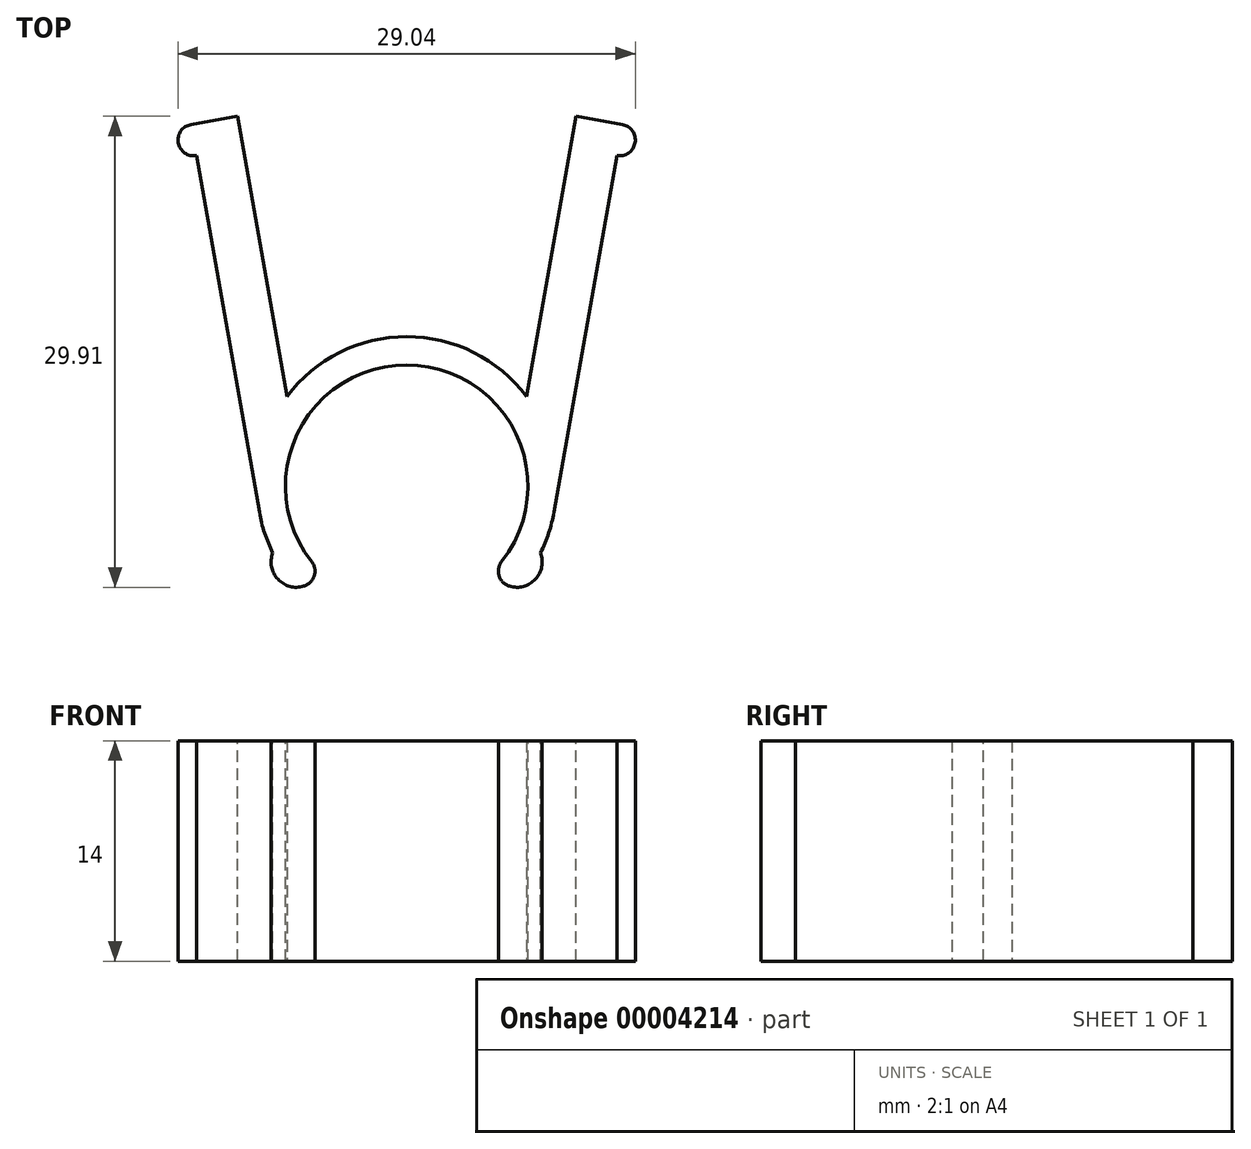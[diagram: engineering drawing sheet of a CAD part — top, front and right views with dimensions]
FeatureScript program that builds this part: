
annotation { "Feature Type Name" : "Feature", "Feature Type Description" : "" }
export const myFeature = defineFeature(function(context is Context, id is Id, definition is map)
    precondition{}
    {
        {
            var Q0;
            Q0=qCreatedBy(makeId("Top.planeOp"),FACE);
            var sketch = newSketch(context, id + "F0", { "sketchPlane" : qUnion([Q0])});
            skCircle(sketch, "E0", {"center": v(0, 0) * mm, "radius": 9.5 * mm});
            skSolve(sketch);
        }
        {
            var Q0;
            Q0=makeQuery(id+"F0.imprint","IMPRINT",FACE,{"disambiguationData":[TD([[makeQuery(id+"F0.imprint","IMPRINT",EDGE,{"derivedFrom":sQuery(id+"F0.wireOp",EDGE,"E0")}),1.0]])]});
            extrude(context, id + "F1", {"entities" : qUnion([Q0]), "depth" : 14 * mm});
        }
        {
            var Q0;
            Q0=makeQuery(id+"F1.opExtrude","CAP_FACE",FACE,{"disambiguationData":[OSD([sQuery(id+"F0.wireOp",EDGE,"E0")])],"isStart":false});
            var sketch = newSketch(context, id + "F2", { "sketchPlane" : qUnion([Q0])});
            skCircle(sketch, "E1", {"center": v(0, 0) * mm, "radius": 7.7 * mm});
            skSolve(sketch);
        }
        {
            var Q0;
            Q0=makeQuery(id+"F2.imprint","IMPRINT",FACE,{"disambiguationData":[TD([[makeQuery(id+"F2.imprint","IMPRINT",EDGE,{"derivedFrom":sQuery(id+"F2.wireOp",EDGE,"E1")}),1.0]])]});
            extrude(context, id + "F3", {"entities" : qUnion([Q0]), "operationType" : NewBodyOperationType.REMOVE, "endBound" : BoundingType.THROUGH_ALL, "oppositeDirection" : true, "depth" : 25 * mm});
        }
        {
            var Q0;
            Q0=qCreatedBy(makeId("Top.planeOp"),FACE);
            var sketch = newSketch(context, id + "F4", { "sketchPlane" : qUnion([Q0])});
            skLineSegment(sketch, "E2.bottom", {"start": v(-7, 0) * mm, "end": v(7, 0) * mm});
            skLineSegment(sketch, "E2.top", {"start": v(-7, -21.3) * mm, "end": v(7, -21.3) * mm});
            skLineSegment(sketch, "E2.left", {"start": v(-7, 0) * mm, "end": v(-7, -21.3) * mm});
            skLineSegment(sketch, "E2.right", {"start": v(7, 0) * mm, "end": v(7, -21.3) * mm});
            skSolve(sketch);
        }
        {
            var Q0;
            Q0=makeQuery(id+"F4.imprint","IMPRINT",FACE,{"disambiguationData":[TD([[makeQuery(id+"F4.imprint","IMPRINT",EDGE,{"derivedFrom":sQuery(id+"F4.wireOp",EDGE,"E2.bottom")}),-1.0]])]});
            extrude(context, id + "F5", {"entities" : qUnion([Q0]), "operationType" : NewBodyOperationType.REMOVE, "endBound" : BoundingType.THROUGH_ALL, "depth" : 25 * mm});
        }
        {
            var Q0;
            Q0=makeQuery(id+"F1.opExtrude","CAP_FACE",FACE,{"disambiguationData":[OSD([sQuery(id+"F0.wireOp",EDGE,"E0")])],"isStart":false});
            var sketch = newSketch(context, id + "F6", { "sketchPlane" : qUnion([Q0])});
            skCircle(sketch, "E3", {"center": v(-7, -4.82) * mm, "radius": 1.6 * mm});
            skCircle(sketch, "E4", {"center": v(7, -4.82) * mm, "radius": 1.6 * mm});
            skSolve(sketch);
        }
        {
            var Q0;
            {var subQ0=sQuery(id+"F0.wireOp",EDGE,"E0");var subQ1=makeQuery(id+"F1.opExtrude","CAP_FACE",FACE,{"disambiguationData":[OSD([subQ0])],"isStart":false});var subQ2=makeQuery(id+"F5.boolean.opBoolean","INTERSECT",EDGE,{"derivedFrom":[subQ1,makeQuery(id+"F5.opExtrude","SWEPT_FACE",FACE,{"disambiguationData":[OSD([sQuery(id+"F4.wireOp",EDGE,"E2.left")])]})]});var subQ3=makeQuery(id+"F6.imprint","IMPRINT",EDGE,{"derivedFrom":subQ2});var subQ4=sQuery(id+"F6.wireOp",EDGE,"E3");var subQ7=makeQuery(id+"F1.opExtrude","CAP_EDGE",EDGE,{"disambiguationData":[OSD([subQ0])],"isStart":false});var subQ9=makeQuery(id+"F5.boolean.opBoolean","INTERSECT",EDGE,{"derivedFrom":[subQ1,makeQuery(id+"F5.opExtrude","SWEPT_FACE",FACE,{"disambiguationData":[OSD([sQuery(id+"F4.wireOp",EDGE,"E2.right")])]})]});var subQ10=makeQuery(id+"F6.imprint","IMPRINT",EDGE,{"derivedFrom":subQ9});var subQ11=sQuery(id+"F6.wireOp",EDGE,"E4");var subQ14=makeQuery(id+"F6.imprint","INTERSECT",VERTEX,{"derivedFrom":[subQ7,subQ4]});var subQ16=makeQuery(id+"F6.imprint","INTERSECT",VERTEX,{"derivedFrom":[subQ7,subQ11]});Q0=qUnion([makeQuery(id+"F6.imprint","IMPRINT",FACE,{"disambiguationData":[TD([[subQ3,-1.0]])]}),makeQuery(id+"F6.imprint","IMPRINT",FACE,{"disambiguationData":[TD([[subQ10,1.0]])]}),makeQuery(id+"F6.imprint","IMPRINT",FACE,{"disambiguationData":[TD([[makeQuery(id+"F6.imprint","IMPRINT",EDGE,{"disambiguationData":[TD([[subQ14,-1.0]])],"derivedFrom":subQ4}),1.0]])]}),makeQuery(id+"F6.imprint","IMPRINT",FACE,{"disambiguationData":[TD([[makeQuery(id+"F6.imprint","IMPRINT",EDGE,{"disambiguationData":[TD([[subQ16,1.0]])],"derivedFrom":subQ11}),1.0]])]}),makeQuery(id+"F6.imprint","IMPRINT",FACE,{"disambiguationData":[TD([[subQ3,1.0]])]}),makeQuery(id+"F6.imprint","IMPRINT",FACE,{"disambiguationData":[TD([[subQ10,-1.0]])]})]);}
            extrude(context, id + "F7", {"entities" : qUnion([Q0]), "operationType" : NewBodyOperationType.ADD, "oppositeDirection" : true, "depth" : 14 * mm});
        }
        {
            var Q0;
            Q0=makeQuery(id+"F7.boolean.opBoolean","MERGE",FACE,{"derivedFrom":[makeQuery(id+"F1.opExtrude","CAP_FACE",FACE,{"disambiguationData":[OSD([sQuery(id+"F0.wireOp",EDGE,"E0")])],"isStart":false}),makeQuery(id+"F7.opExtrude","CAP_FACE",FACE,{"disambiguationData":[OSD([sQuery(id+"F6.wireOp",EDGE,"E3")])],"isStart":true}),makeQuery(id+"F7.opExtrude","CAP_FACE",FACE,{"disambiguationData":[OSD([sQuery(id+"F6.wireOp",EDGE,"E4")])],"isStart":true})]});
            var sketch = newSketch(context, id + "F8", { "sketchPlane" : qUnion([Q0])});
            skCircle(sketch, "E5", {"center": v(0, 0) * mm, "radius": 7.7 * mm});
            skSolve(sketch);
        }
        {
            var Q0;
            {var subQ3=makeQuery(id+"F1.opExtrude","CAP_EDGE",EDGE,{"disambiguationData":[OSD([sQuery(id+"F0.wireOp",EDGE,"E0")])],"isStart":false});Q0=makeQuery(id+"F8.imprint","IMPRINT",FACE,{"disambiguationData":[TD([[makeQuery(id+"F8.imprint","IMPRINT",EDGE,{"derivedFrom":subQ3}),1.0]])]});}
            var sketch = newSketch(context, id + "F9", { "sketchPlane" : qUnion([Q0])});
            skLineSegment(sketch, "E6.bottom", {"start": v(-9.36, -1.65) * mm, "end": v(-6.4, -1.13) * mm});
            skLineSegment(sketch, "E6.top", {"start": v(-13.7, 22.97) * mm, "end": v(-10.74, 23.5) * mm});
            skLineSegment(sketch, "E6.left", {"start": v(-9.36, -1.65) * mm, "end": v(-13.7, 22.97) * mm});
            skLineSegment(sketch, "E6.right", {"start": v(-6.4, -1.13) * mm, "end": v(-10.74, 23.5) * mm});
            skLineSegment(sketch, "E7.bottom", {"start": v(10.74, 23.5) * mm, "end": v(13.7, 22.97) * mm});
            skLineSegment(sketch, "E7.top", {"start": v(6.4, -1.13) * mm, "end": v(9.36, -1.65) * mm});
            skLineSegment(sketch, "E7.left", {"start": v(10.74, 23.5) * mm, "end": v(6.4, -1.13) * mm});
            skLineSegment(sketch, "E7.right", {"start": v(13.7, 22.97) * mm, "end": v(9.36, -1.65) * mm});
            skSolve(sketch);
        }
        {
            var Q0;
            Q0 = qSketchRegion(id + "F9", true);
            extrude(context, id + "F10", {"entities" : qUnion([Q0]), "operationType" : NewBodyOperationType.ADD, "oppositeDirection" : true, "depth" : 14 * mm});
        }
        {
            var Q0;
            {var subQ0=makeQuery(id+"F7.opExtrude","CAP_EDGE",EDGE,{"disambiguationData":[OSD([sQuery(id+"F6.wireOp",EDGE,"E3")])],"isStart":true});var subQ1=sQuery(id+"F8.wireOp",EDGE,"E5");var subQ2=makeQuery(id+"F8.imprint","INTERSECT",VERTEX,{"disambiguationData":[OD(1.0)],"derivedFrom":[subQ0,subQ1]});var subQ3=makeQuery(id+"F8.imprint","INTERSECT",VERTEX,{"disambiguationData":[OD(0.0)],"derivedFrom":[subQ0,subQ1]});var subQ5=makeQuery(id+"F7.opExtrude","CAP_EDGE",EDGE,{"disambiguationData":[OSD([sQuery(id+"F6.wireOp",EDGE,"E4")])],"isStart":true});var subQ7=makeQuery(id+"F8.imprint","INTERSECT",VERTEX,{"disambiguationData":[OD(0.0)],"derivedFrom":[subQ5,subQ1]});Q0=qUnion([makeQuery(id+"F8.imprint","IMPRINT",FACE,{"disambiguationData":[TD([[makeQuery(id+"F8.imprint","IMPRINT",EDGE,{"disambiguationData":[TD([[subQ3,-1.0]])],"derivedFrom":subQ1}),1.0]])]}),makeQuery(id+"F8.imprint","IMPRINT",FACE,{"disambiguationData":[TD([[makeQuery(id+"F8.imprint","IMPRINT",EDGE,{"disambiguationData":[TD([[subQ7,1.0]])],"derivedFrom":subQ1}),1.0]])]}),makeQuery(id+"F8.imprint","IMPRINT",FACE,{"disambiguationData":[TD([[makeQuery(id+"F8.imprint","IMPRINT",EDGE,{"disambiguationData":[TD([[subQ2,-1.0]])],"derivedFrom":subQ1}),1.0]])]})]);}
            extrude(context, id + "F11", {"entities" : qUnion([Q0]), "operationType" : NewBodyOperationType.REMOVE, "endBound" : BoundingType.THROUGH_ALL, "oppositeDirection" : true, "depth" : 25 * mm});
        }
        {
            var Q0;
            Q0=makeQuery(id+"F11.boolean.opBoolean","INTERSECT",EDGE,{"derivedFrom":[makeQuery(id+"F7.opExtrude","SWEPT_FACE",FACE,{"disambiguationData":[OSD([sQuery(id+"F6.wireOp",EDGE,"E3")])]}),makeQuery(id+"F11.opExtrude","SWEPT_FACE",FACE,{"disambiguationData":[OSD([sQuery(id+"F8.wireOp",EDGE,"E5")])]})]});
            var Q1;
            Q1=makeQuery(id+"F11.boolean.opBoolean","INTERSECT",EDGE,{"derivedFrom":[makeQuery(id+"F7.opExtrude","SWEPT_FACE",FACE,{"disambiguationData":[OSD([sQuery(id+"F6.wireOp",EDGE,"E4")])]}),makeQuery(id+"F11.opExtrude","SWEPT_FACE",FACE,{"disambiguationData":[OSD([sQuery(id+"F8.wireOp",EDGE,"E5")])]})]});
            fillet(context, id + "F12", {"entities" : qUnion([Q0, Q1]), "radius" : 1 * mm, "tangentPropagation" : true, "allowEdgeOverflow" : false});
        }
        {
            var Q0;
            Q0=makeQuery(id+"F10.boolean.opBoolean","MERGE",FACE,{"derivedFrom":[makeQuery(id+"F7.boolean.opBoolean","MERGE",FACE,{"derivedFrom":[makeQuery(id+"F1.opExtrude","CAP_FACE",FACE,{"disambiguationData":[OSD([sQuery(id+"F0.wireOp",EDGE,"E0")])],"isStart":false}),makeQuery(id+"F7.opExtrude","CAP_FACE",FACE,{"disambiguationData":[OSD([sQuery(id+"F6.wireOp",EDGE,"E3")])],"isStart":true}),makeQuery(id+"F7.opExtrude","CAP_FACE",FACE,{"disambiguationData":[OSD([sQuery(id+"F6.wireOp",EDGE,"E4")])],"isStart":true})]}),makeQuery(id+"F10.opExtrude","CAP_FACE",FACE,{"disambiguationData":[OSD([sQuery(id+"F9.wireOp",EDGE,"E6.bottom"),sQuery(id+"F9.wireOp",EDGE,"E6.top"),sQuery(id+"F9.wireOp",EDGE,"E6.left"),sQuery(id+"F9.wireOp",EDGE,"E6.right")])],"isStart":true}),makeQuery(id+"F10.opExtrude","CAP_FACE",FACE,{"disambiguationData":[OSD([sQuery(id+"F9.wireOp",EDGE,"E7.bottom"),sQuery(id+"F9.wireOp",EDGE,"E7.top"),sQuery(id+"F9.wireOp",EDGE,"E7.left"),sQuery(id+"F9.wireOp",EDGE,"E7.right")])],"isStart":true})]});
            var sketch = newSketch(context, id + "F13", { "sketchPlane" : qUnion([Q0])});
            skCircle(sketch, "E8", {"center": v(-13.52, 21.99) * mm, "radius": 1 * mm});
            skCircle(sketch, "E9", {"center": v(13.52, 21.99) * mm, "radius": 1 * mm});
            skSolve(sketch);
        }
        {
            var Q0;
            {var subQ0=makeQuery(id+"F10.opExtrude","CAP_EDGE",EDGE,{"disambiguationData":[OSD([sQuery(id+"F9.wireOp",EDGE,"E6.left")])],"isStart":true});var subQ1=sQuery(id+"F13.wireOp",EDGE,"E8");var subQ2=makeQuery(id+"F13.imprint","INTERSECT",VERTEX,{"derivedFrom":[subQ0,subQ1]});var subQ5=makeQuery(id+"F10.opExtrude","CAP_EDGE",EDGE,{"disambiguationData":[OSD([sQuery(id+"F9.wireOp",EDGE,"E7.right")])],"isStart":true});var subQ6=sQuery(id+"F13.wireOp",EDGE,"E9");var subQ7=makeQuery(id+"F13.imprint","INTERSECT",VERTEX,{"derivedFrom":[subQ5,subQ6]});Q0=qUnion([makeQuery(id+"F13.imprint","IMPRINT",FACE,{"disambiguationData":[TD([[makeQuery(id+"F13.imprint","IMPRINT",EDGE,{"disambiguationData":[TD([[subQ2,1.0]])],"derivedFrom":subQ1}),1.0]])]}),makeQuery(id+"F13.imprint","IMPRINT",FACE,{"disambiguationData":[TD([[makeQuery(id+"F13.imprint","IMPRINT",EDGE,{"disambiguationData":[TD([[subQ7,-1.0]])],"derivedFrom":subQ6}),1.0]])]}),makeQuery(id+"F13.imprint","IMPRINT",FACE,{"disambiguationData":[TD([[makeQuery(id+"F13.imprint","IMPRINT",EDGE,{"disambiguationData":[TD([[subQ2,-1.0]])],"derivedFrom":subQ1}),1.0]])]}),makeQuery(id+"F13.imprint","IMPRINT",FACE,{"disambiguationData":[TD([[makeQuery(id+"F13.imprint","IMPRINT",EDGE,{"disambiguationData":[TD([[subQ7,1.0]])],"derivedFrom":subQ6}),1.0]])]})]);}
            extrude(context, id + "F14", {"entities" : qUnion([Q0]), "operationType" : NewBodyOperationType.ADD, "oppositeDirection" : true, "depth" : 14 * mm});
        }
    });
